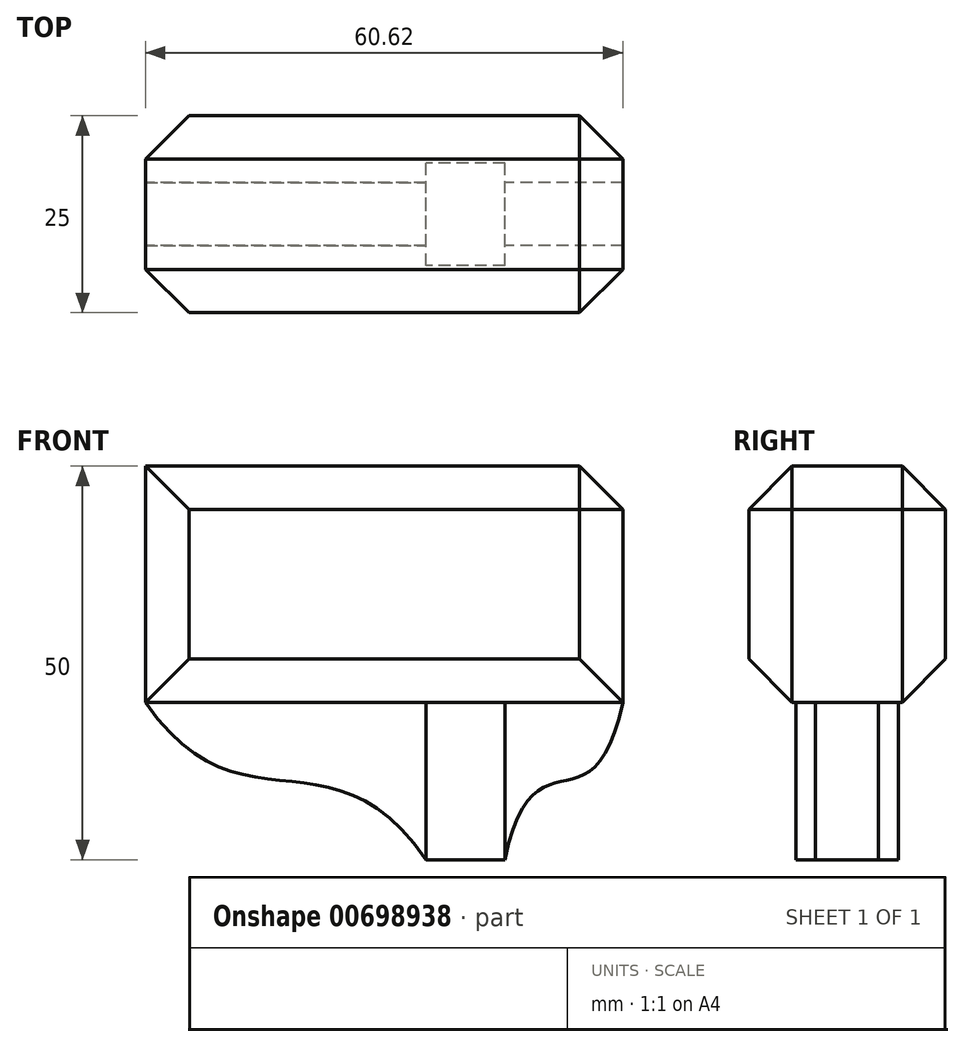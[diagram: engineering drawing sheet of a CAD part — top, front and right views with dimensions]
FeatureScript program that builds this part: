
annotation { "Feature Type Name" : "Feature", "Feature Type Description" : "" }
export const myFeature = defineFeature(function(context is Context, id is Id, definition is map)
    precondition{}
    {
        {
            var Q0;
            Q0=qCreatedBy(makeId("Front.planeOp"),FACE);
            var sketch = newSketch(context, id + "F0", { "sketchPlane" : qUnion([Q0])});
            skLineSegment(sketch, "E0.bottom", {"start": v(-56.56, 7.93) * mm, "end": v(-117.18, 7.93) * mm});
            skLineSegment(sketch, "E0.top", {"start": v(-56.56, 37.93) * mm, "end": v(-117.18, 37.93) * mm});
            skLineSegment(sketch, "E0.left", {"start": v(-56.56, 7.93) * mm, "end": v(-56.56, 37.93) * mm});
            skLineSegment(sketch, "E0.right", {"start": v(-117.18, 7.93) * mm, "end": v(-117.18, 37.93) * mm});
            skPoint(sketch, "E0.middle", {"position": v(-86.87, 22.93) * mm});
            skLineSegment(sketch, "E1.bottom", {"start": v(-71.56, 7.93) * mm, "end": v(-81.56, 7.93) * mm});
            skLineSegment(sketch, "E1.top", {"start": v(-71.56, -12.07) * mm, "end": v(-81.56, -12.07) * mm});
            skLineSegment(sketch, "E1.left", {"start": v(-71.56, 7.93) * mm, "end": v(-71.56, -12.07) * mm});
            skLineSegment(sketch, "E1.right", {"start": v(-81.56, 7.93) * mm, "end": v(-81.56, -12.07) * mm});
            skPoint(sketch, "E1.middle", {"position": v(-76.56, -2.07) * mm});
            skFitSpline(sketch, "E2", {"points": [v(-56.56, 7.93) * mm, v(-71.56, -12.07) * mm], "startDerivative": vector(-11.04, -52.3) * mm, "endDerivative": vector(-11.04, -52.3) * mm});
            skFitSpline(sketch, "E3", {"points": [v(-117.18, 7.93) * mm, v(-81.56, -12.07) * mm], "startDerivative": vector(35.63, -52.3) * mm, "endDerivative": vector(35.63, -52.3) * mm});
            skLineSegment(sketch, "E4", {"start": v(-76.56, -12.07) * mm, "end": v(-76.56, 37.93) * mm});
            skSolve(sketch);
        }
        {
            var Q0;
            {var subQ2=sQuery(id+"F0.wireOp",EDGE,"E1.left");Q0=makeQuery(id+"F0.imprint","IMPRINT",FACE,{"disambiguationData":[TD([[makeQuery(id+"F0.imprint","IMPRINT",EDGE,{"derivedFrom":subQ2}),1.0]])]});}
            var Q1;
            {var subQ2=sQuery(id+"F0.wireOp",EDGE,"E1.right");Q1=makeQuery(id+"F0.imprint","IMPRINT",FACE,{"disambiguationData":[TD([[makeQuery(id+"F0.imprint","IMPRINT",EDGE,{"derivedFrom":subQ2}),-1.0]])]});}
            extrude(context, id + "F1", {"entities" : qUnion([Q0, Q1]), "endBound" : BoundingType.SYMMETRIC, "depth" : 8 * mm, "offsetDistance" : 25 * mm});
        }
        {
            var Q0;
            {var subQ0=sQuery(id+"F0.wireOp",EDGE,"E1.right");Q0=makeQuery(id+"F0.imprint","IMPRINT",FACE,{"disambiguationData":[TD([[makeQuery(id+"F0.imprint","IMPRINT",EDGE,{"derivedFrom":subQ0}),1.0]])]});}
            var Q1;
            {var subQ0=sQuery(id+"F0.wireOp",EDGE,"E1.left");Q1=makeQuery(id+"F0.imprint","IMPRINT",FACE,{"disambiguationData":[TD([[makeQuery(id+"F0.imprint","IMPRINT",EDGE,{"derivedFrom":subQ0}),-1.0]])]});}
            extrude(context, id + "F2", {"entities" : qUnion([Q0, Q1]), "endBound" : BoundingType.SYMMETRIC, "depth" : 13 * mm, "offsetDistance" : 25 * mm});
        }
        {
            var Q0;
            {var subQ5=sQuery(id+"F0.wireOp",EDGE,"E0.right");Q0=makeQuery(id+"F0.imprint","IMPRINT",FACE,{"disambiguationData":[TD([[makeQuery(id+"F0.imprint","IMPRINT",EDGE,{"derivedFrom":subQ5}),-1.0]])]});}
            var Q1;
            {var subQ5=sQuery(id+"F0.wireOp",EDGE,"E0.left");Q1=makeQuery(id+"F0.imprint","IMPRINT",FACE,{"disambiguationData":[TD([[makeQuery(id+"F0.imprint","IMPRINT",EDGE,{"derivedFrom":subQ5}),1.0]])]});}
            extrude(context, id + "F3", {"entities" : qUnion([Q0, Q1]), "endBound" : BoundingType.SYMMETRIC, "depth" : 25 * mm, "offsetDistance" : 25 * mm});
        }
        {
            var Q0;
            Q0=makeQuery(id+"F3.opExtrude","SWEPT_EDGE",EDGE,{"disambiguationData":[OSD([sQuery(id+"F0.wireOp",EDGE,"E0.top"),sQuery(id+"F0.wireOp",EDGE,"E0.left")])]});
            var Q1;
            Q1=makeQuery(id+"F3.opExtrude","CAP_EDGE",EDGE,{"disambiguationData":[OSD([sQuery(id+"F0.wireOp",EDGE,"E0.left")])],"isStart":false});
            var Q2;
            Q2=makeQuery(id+"F3.opExtrude","CAP_EDGE",EDGE,{"disambiguationData":[OSD([sQuery(id+"F0.wireOp",EDGE,"E0.top")])],"isStart":false});
            var Q3;
            Q3=makeQuery(id+"F3.opExtrude","CAP_EDGE",EDGE,{"disambiguationData":[OSD([sQuery(id+"F0.wireOp",EDGE,"E0.top")])],"isStart":true});
            var Q4;
            Q4=makeQuery(id+"F3.opExtrude","CAP_EDGE",EDGE,{"disambiguationData":[OSD([sQuery(id+"F0.wireOp",EDGE,"E0.left")])],"isStart":true});
            var Q5;
            Q5=makeQuery(id+"F3.opExtrude","CAP_EDGE",EDGE,{"disambiguationData":[OSD([sQuery(id+"F0.wireOp",EDGE,"E0.right")])],"isStart":true});
            var Q6;
            Q6=makeQuery(id+"F3.opExtrude","CAP_EDGE",EDGE,{"disambiguationData":[OSD([sQuery(id+"F0.wireOp",EDGE,"E0.right")])],"isStart":false});
            var Q7;
            Q7=makeQuery(id+"F3.opExtrude","CAP_EDGE",EDGE,{"disambiguationData":[OSD([sQuery(id+"F0.wireOp",EDGE,"E0.bottom"),sQuery(id+"F0.wireOp",EDGE,"E1.bottom")])],"isStart":false});
            var Q8;
            Q8=makeQuery(id+"F3.opExtrude","CAP_EDGE",EDGE,{"disambiguationData":[OSD([sQuery(id+"F0.wireOp",EDGE,"E0.bottom"),sQuery(id+"F0.wireOp",EDGE,"E1.bottom")])],"isStart":true});
            chamfer(context, id + "F4", {"entities" : qUnion([Q0, Q1, Q2, Q3, Q4, Q5, Q6, Q7, Q8]), "width" : 5.5 * mm, "tangentPropagation" : true});
        }
    });
